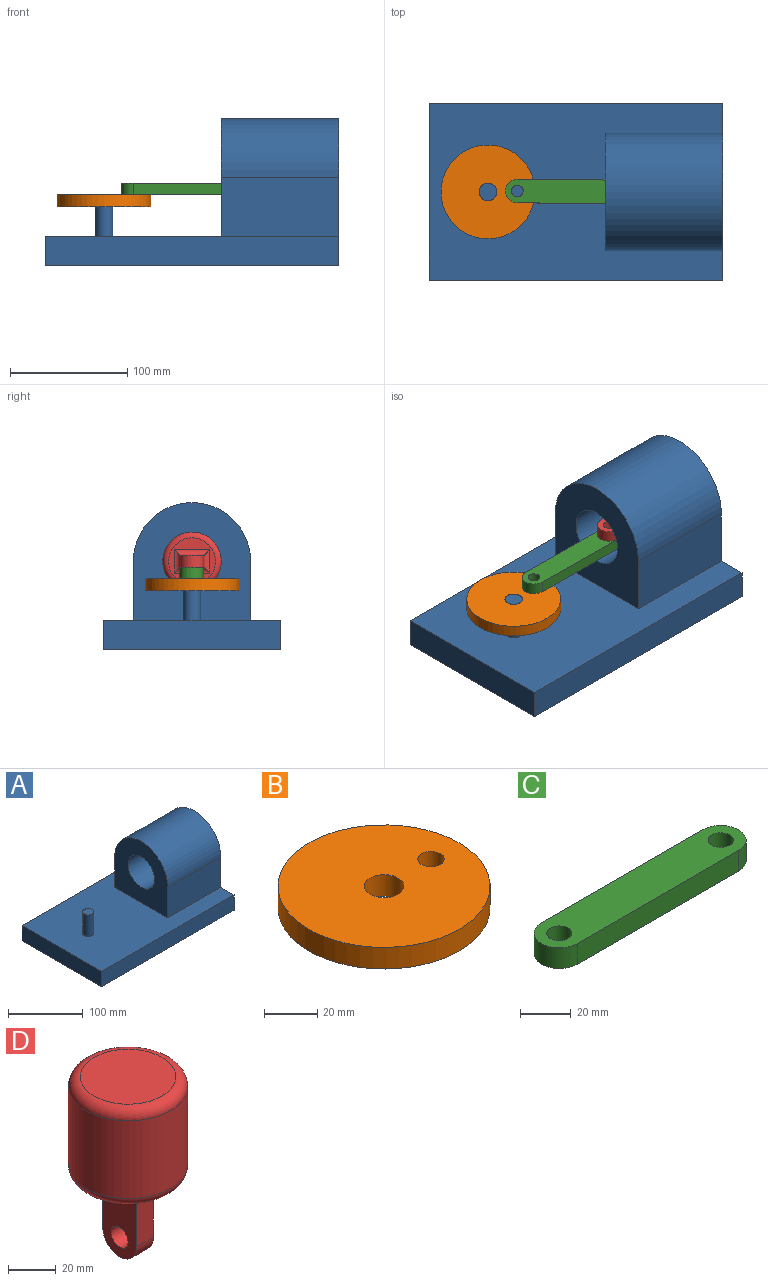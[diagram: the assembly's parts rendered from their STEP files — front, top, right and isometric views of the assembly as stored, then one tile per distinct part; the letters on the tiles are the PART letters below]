
ASSEMBLY  parts=4 mates=4
PART A: 13 faces, bbox 250x150x125 mm
  f0: plane 250x150mm, normal (0,0,1), area 27323.3mm2, adj f1,f2,f3,f4,f6,f8,f9,f10
  f1: plane 150x125mm, normal (1,0,0), area 10713.5mm2, adj f0,f2,f4,f5,f8,f10,f11,f12
  f2: plane 250x25mm, normal (0,1,0), area 6250mm2, adj f0,f1,f3,f5
  f3: plane 150x25mm, normal (-1,0,0), area 3750mm2, adj f0,f2,f4,f5
  f4: plane 250x25mm, normal (0,-1,0), area 6250mm2, adj f0,f1,f3,f5
  f5: plane 250x150mm, normal (0,0,-1), area 37500mm2, adj f1,f2,f3,f4
  f6: cylinder r=7.5mm len=35mm, axis (0,0,-1), area 1649.3mm2, adj f0,f7
  f7: plane 15x15mm, normal (0,0,1), area 176.7mm2, adj f6
  f8: plane 100x50mm, normal (0,1,0), area 5000mm2, adj f0,f1,f9,f12
  f9: plane 100x100mm, normal (-1,0,0), area 6963.5mm2, adj f0,f8,f10,f11,f12
  f10: plane 100x50mm, normal (0,-1,0), area 5000mm2, adj f0,f1,f9,f12
  f11: cylinder r=25mm len=100mm, axis (-1,0,0), area 15708mm2, adj f1,f9
  f12: cylinder r=50mm len=100mm, axis (-1,0,0), area 15708mm2, adj f1,f8,f9,f10
PART B: 5 faces, bbox 80x80x10 mm
  f0: cylinder r=40mm len=80mm, axis (0,0,-1), area 2513.3mm2, adj f1,f2
  f1: plane 80x80mm, normal (0,0,1), area 4771.3mm2, adj f0,f3,f4
  f2: plane 80x80mm, normal (0,0,-1), area 4771.3mm2, adj f0,f3,f4
  f3: cylinder r=5mm len=10mm, axis (0,0,1), area 314.2mm2, adj f1,f2
  f4: cylinder r=7.5mm len=15mm, axis (0,0,1), area 471.2mm2, adj f1,f2
PART C: 8 faces, bbox 110x20x10 mm
  f0: plane 90x10mm, normal (0,-1,0), area 900mm2, adj f1,f5,f6,f7
  f1: cylinder r=10mm len=20mm, axis (0,0,-1), area 314.2mm2, adj f0,f2,f6,f7
  f2: plane 90x10mm, normal (0,1,0), area 900mm2, adj f1,f5,f6,f7
  f3: cylinder r=5mm len=10mm, axis (0,0,-1), area 314.2mm2, adj f6,f7
  f4: cylinder r=5mm len=10mm, axis (0,0,-1), area 314.2mm2, adj f6,f7
  f5: cylinder r=10mm len=20mm, axis (0,0,-1), area 314.2mm2, adj f0,f2,f6,f7
  f6: plane 110x20mm, normal (0,0,1), area 1957.1mm2, adj f0,f1,f2,f3,f4,f5
  f7: plane 110x20mm, normal (0,0,-1), area 1957.1mm2, adj f0,f1,f2,f3,f4,f5
PART D: 15 faces, bbox 54.1x54.1x90 mm
  f0: plane 40x40mm, normal (0,0,-1), area 656.6mm2, adj f8,f9,f10,f11,f12
  f1: cylinder r=25mm len=50mm, axis (0,0,-1), area 6283.2mm2, adj f12,f13
  f2: plane 40x40mm, normal (0,0,1), area 1256.6mm2, adj f13
  f3: plane 35x20mm, normal (1,0,0), area 578.5mm2, adj f4,f6,f7,f8,f14
  f4: plane 25x10mm, normal (0,-1,0), area 250mm2, adj f3,f5,f7,f10
  f5: plane 35x20mm, normal (-1,0,0), area 578.5mm2, adj f4,f6,f7,f11,f14
  f6: plane 25x10mm, normal (0,1,0), area 250mm2, adj f3,f5,f7,f9
  f7: cylinder r=10mm len=20mm, axis (-1,0,0), area 314.2mm2, adj f3,f4,f5,f6
  f8: cylinder r=5mm len=30mm, axis (0,1,0), area 185.6mm2, adj f0,f3,f9,f10
  f9: cylinder r=5mm len=20mm, axis (-1,0,0), area 107.1mm2, adj f0,f6,f8,f11
  f10: cylinder r=5mm len=20mm, axis (1,0,0), area 107.1mm2, adj f0,f4,f8,f11
  f11: cylinder r=5mm len=30mm, axis (0,-1,0), area 185.6mm2, adj f0,f5,f9,f10
  f12: torus R=20mm, axis (0,0,1), area 1144mm2, adj f0,f1
  f13: torus R=20mm, axis (0,0,1), area 1144mm2, adj f1,f2
  f14: cylinder r=5mm len=10mm, axis (-1,0,0), area 314.2mm2, adj f3,f5
PLACE A at identity fixed
PLACE B rot(axis=(0,0,1),1.5deg) t=(-75,0,50)mm
PLACE C rot(axis=(0,0,-1),0.4deg) t=(-5.01,0.33,60)mm
PLACE D rot(axis=(0,1,0),90deg) t=(69.99,0,75)mm
MATE revolute A.f6 <-> B.f4  axis (0,0,1) through (-75,0,60)mm
MATE revolute C.f4 <-> D.f14  axis (0,0,-1) through (39.99,0,70)mm
MATE revolute C.f3 <-> B.f3  axis (0,0,-1) through (-50.01,0.67,60)mm
MATE slider D.f1 <-> A.f11  axis (1,0,0) through (119.99,0,75)mm
